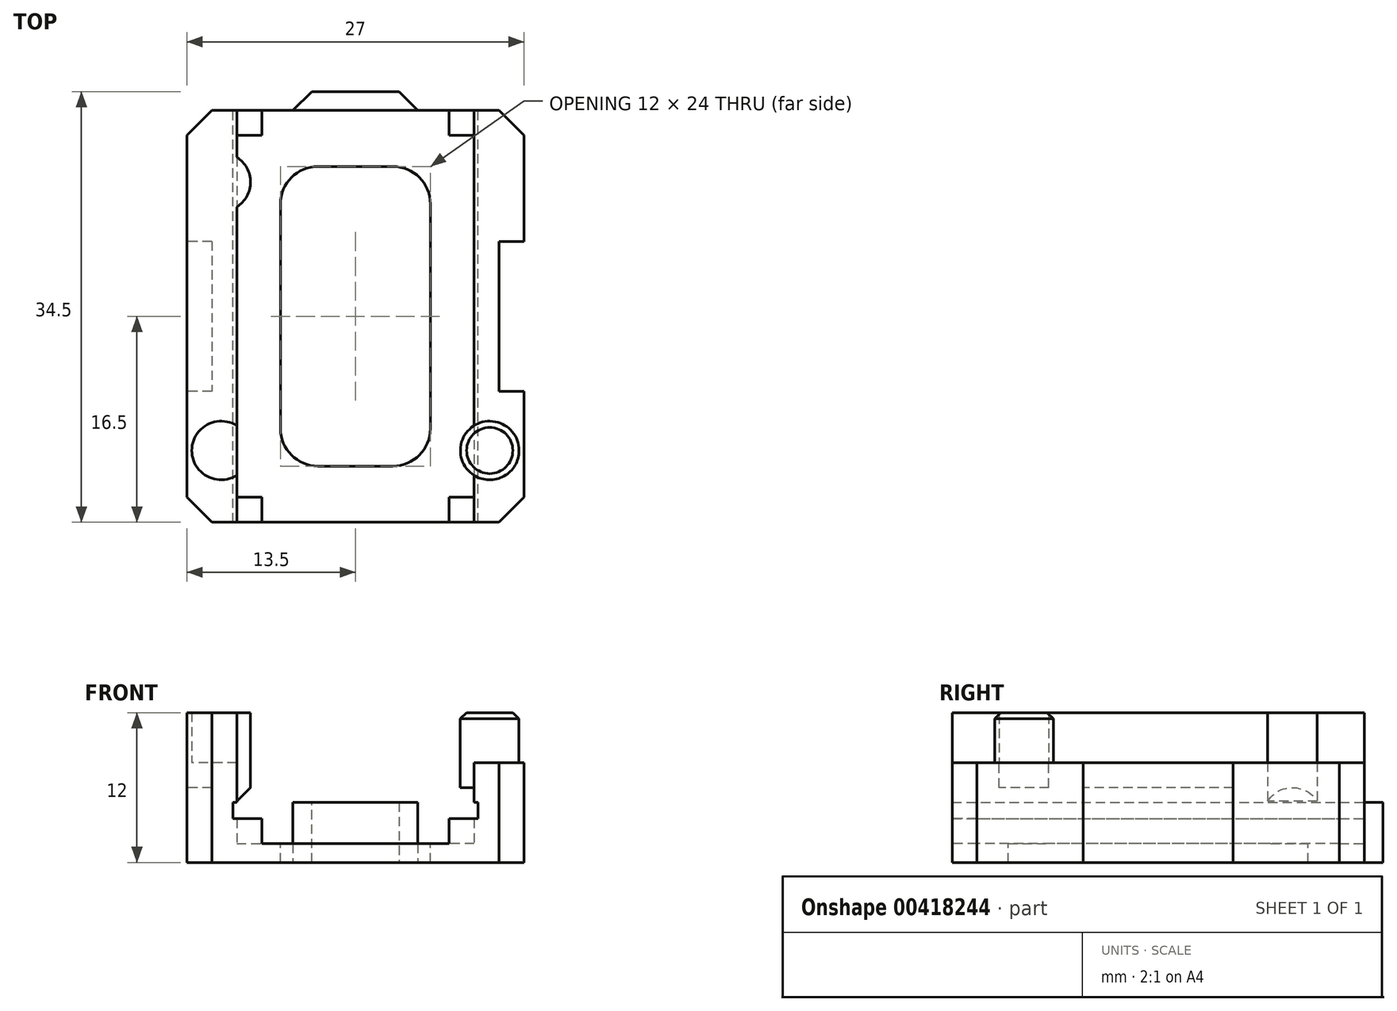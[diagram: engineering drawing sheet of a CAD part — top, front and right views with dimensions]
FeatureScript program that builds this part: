
annotation { "Feature Type Name" : "Feature", "Feature Type Description" : "" }
export const myFeature = defineFeature(function(context is Context, id is Id, definition is map)
    precondition{}
    {
        {
            var Q0;
            Q0=qCreatedBy(makeId("Top.planeOp"),FACE);
            var sketch = newSketch(context, id + "F0", { "sketchPlane" : qUnion([Q0])});
            skLineSegment(sketch, "E0.bottom", {"start": v(13.5, 16.5) * mm, "end": v(-13.5, 16.5) * mm});
            skLineSegment(sketch, "E0.top", {"start": v(13.5, -16.5) * mm, "end": v(-13.5, -16.5) * mm});
            skLineSegment(sketch, "E0.left", {"start": v(13.5, 16.5) * mm, "end": v(13.5, -16.5) * mm});
            skLineSegment(sketch, "E0.right", {"start": v(-13.5, 16.5) * mm, "end": v(-13.5, -16.5) * mm});
            skPoint(sketch, "E0.middle", {"position": v(0, 0) * mm});
            skLineSegment(sketch, "E1", {"start": v(-9.5, 16.5) * mm, "end": v(-9.5, -16.5) * mm});
            skLineSegment(sketch, "E2.MirrorCS", {"start": v(9.5, 16.5) * mm, "end": v(9.5, -16.5) * mm});
            skLineSegment(sketch, "E3", {"start": v(-5, 16.5) * mm, "end": v(-5, 18) * mm});
            skLineSegment(sketch, "E4", {"start": v(-5, 18) * mm, "end": v(0, 18) * mm});
            skLineSegment(sketch, "E5.MirrorCS", {"start": v(5, 18) * mm, "end": v(0, 18) * mm});
            skLineSegment(sketch, "E6.MirrorCS", {"start": v(5, 16.5) * mm, "end": v(5, 18) * mm});
            skSolve(sketch);
        }
        {
            var Q0;
            {var subQ0=sQuery(id+"F0.wireOp",EDGE,"E1");Q0=makeQuery(id+"F0.imprint","IMPRINT",FACE,{"disambiguationData":[TD([[makeQuery(id+"F0.imprint","IMPRINT",EDGE,{"derivedFrom":subQ0}),1.0]])]});}
            extrude(context, id + "F1", {"entities" : qUnion([Q0]), "depth" : 1.5 * mm});
        }
        {
            var Q0;
            {var subQ0=sQuery(id+"F0.wireOp",EDGE,"E0.right");Q0=makeQuery(id+"F0.imprint","IMPRINT",FACE,{"disambiguationData":[TD([[makeQuery(id+"F0.imprint","IMPRINT",EDGE,{"derivedFrom":subQ0}),1.0]])]});}
            var Q1;
            {var subQ0=sQuery(id+"F0.wireOp",EDGE,"E0.left");Q1=makeQuery(id+"F0.imprint","IMPRINT",FACE,{"disambiguationData":[TD([[makeQuery(id+"F0.imprint","IMPRINT",EDGE,{"derivedFrom":subQ0}),-1.0]])]});}
            extrude(context, id + "F2", {"entities" : qUnion([Q0, Q1]), "operationType" : NewBodyOperationType.ADD, "depth" : 8 * mm});
        }
        {
            var Q0;
            Q0=makeQuery(id+"F2.opExtrude","SWEPT_FACE",FACE,{"disambiguationData":[OSD([sQuery(id+"F0.wireOp",EDGE,"E1")])]});
            var sketch = newSketch(context, id + "F3", { "sketchPlane" : qUnion([Q0])});
            skLineSegment(sketch, "E7", {"start": v(-16.5, 3.5) * mm, "end": v(16.5, 3.5) * mm});
            skLineSegment(sketch, "E8", {"start": v(-16.5, 5) * mm, "end": v(16.5, 5) * mm});
            skSolve(sketch);
        }
        {
            var Q0;
            {var subQ0=sQuery(id+"F3.wireOp",EDGE,"E7");Q0=makeQuery(id+"F3.imprint","IMPRINT",FACE,{"disambiguationData":[TD([[makeQuery(id+"F3.imprint","IMPRINT",EDGE,{"derivedFrom":subQ0}),1.0]])]});}
            extrude(context, id + "F4", {"entities" : qUnion([Q0]), "operationType" : NewBodyOperationType.REMOVE, "oppositeDirection" : true, "depth" : 0.5 * mm});
        }
        {
            var Q0;
            Q0=makeQuery(id+"F2.opExtrude","SWEPT_FACE",FACE,{"disambiguationData":[OSD([sQuery(id+"F0.wireOp",EDGE,"E2.MirrorCS")])]});
            var sketch = newSketch(context, id + "F5", { "sketchPlane" : qUnion([Q0])});
            skLineSegment(sketch, "E9", {"start": v(16.5, 3.5) * mm, "end": v(-16.5, 3.5) * mm});
            skLineSegment(sketch, "E10", {"start": v(16.5, 5) * mm, "end": v(-16.5, 5) * mm});
            skSolve(sketch);
        }
        {
            var Q0;
            {var subQ0=sQuery(id+"F5.wireOp",EDGE,"E9");Q0=makeQuery(id+"F5.imprint","IMPRINT",FACE,{"disambiguationData":[TD([[makeQuery(id+"F5.imprint","IMPRINT",EDGE,{"derivedFrom":subQ0}),-1.0]])]});}
            extrude(context, id + "F6", {"entities" : qUnion([Q0]), "operationType" : NewBodyOperationType.REMOVE, "oppositeDirection" : true, "depth" : 0.5 * mm});
        }
        {
            var Q0;
            Q0=makeQuery(id+"F1.opExtrude","CAP_FACE",FACE,{"disambiguationData":[OSD([sQuery(id+"F0.wireOp",EDGE,"E0.bottom"),sQuery(id+"F0.wireOp",EDGE,"E0.top"),sQuery(id+"F0.wireOp",EDGE,"E1"),sQuery(id+"F0.wireOp",EDGE,"E2.MirrorCS")])],"isStart":false});
            var sketch = newSketch(context, id + "F7", { "sketchPlane" : qUnion([Q0])});
            skLineSegment(sketch, "E11", {"start": v(-9.5, 14.5) * mm, "end": v(-7.5, 14.5) * mm});
            skLineSegment(sketch, "E12", {"start": v(-7.5, 14.5) * mm, "end": v(-7.5, 16.5) * mm});
            skLineSegment(sketch, "E13.MirrorCS", {"start": v(7.5, 14.5) * mm, "end": v(7.5, 16.5) * mm});
            skLineSegment(sketch, "E14.MirrorCS", {"start": v(9.5, 14.5) * mm, "end": v(7.5, 14.5) * mm});
            skLineSegment(sketch, "E15.MirrorCS", {"start": v(-9.5, -14.5) * mm, "end": v(-7.5, -14.5) * mm});
            skLineSegment(sketch, "E16.MirrorCS", {"start": v(-7.5, -14.5) * mm, "end": v(-7.5, -16.5) * mm});
            skLineSegment(sketch, "E17.MirrorCS", {"start": v(7.5, -14.5) * mm, "end": v(7.5, -16.5) * mm});
            skLineSegment(sketch, "E18.MirrorCS", {"start": v(9.5, -14.5) * mm, "end": v(7.5, -14.5) * mm});
            skSolve(sketch);
        }
        {
            var Q0;
            {var subQ0=sQuery(id+"F7.wireOp",EDGE,"E11");Q0=makeQuery(id+"F7.imprint","IMPRINT",FACE,{"disambiguationData":[TD([[makeQuery(id+"F7.imprint","IMPRINT",EDGE,{"derivedFrom":subQ0}),1.0]])]});}
            var Q1;
            {var subQ0=sQuery(id+"F7.wireOp",EDGE,"E13.MirrorCS");Q1=makeQuery(id+"F7.imprint","IMPRINT",FACE,{"disambiguationData":[TD([[makeQuery(id+"F7.imprint","IMPRINT",EDGE,{"derivedFrom":subQ0}),-1.0]])]});}
            var Q2;
            {var subQ0=sQuery(id+"F7.wireOp",EDGE,"E17.MirrorCS");Q2=makeQuery(id+"F7.imprint","IMPRINT",FACE,{"disambiguationData":[TD([[makeQuery(id+"F7.imprint","IMPRINT",EDGE,{"derivedFrom":subQ0}),1.0]])]});}
            var Q3;
            {var subQ0=sQuery(id+"F7.wireOp",EDGE,"E15.MirrorCS");Q3=makeQuery(id+"F7.imprint","IMPRINT",FACE,{"disambiguationData":[TD([[makeQuery(id+"F7.imprint","IMPRINT",EDGE,{"derivedFrom":subQ0}),-1.0]])]});}
            extrude(context, id + "F8", {"entities" : qUnion([Q0, Q1, Q2, Q3]), "operationType" : NewBodyOperationType.ADD, "depth" : 2 * mm});
        }
        {
            var Q0;
            Q0=makeQuery(id+"F2.opExtrude","CAP_FACE",FACE,{"disambiguationData":[OSD([sQuery(id+"F0.wireOp",EDGE,"E0.bottom"),sQuery(id+"F0.wireOp",EDGE,"E0.top"),sQuery(id+"F0.wireOp",EDGE,"E0.right"),sQuery(id+"F0.wireOp",EDGE,"E1")])],"isStart":false});
            var sketch = newSketch(context, id + "F9", { "sketchPlane" : qUnion([Q0])});
            skPoint(sketch, "E19.middle", {"position": v(0, 0) * mm});
            skCircle(sketch, "E20", {"center": v(-10.75, 10.75) * mm, "radius": 2.35 * mm});
            skCircle(sketch, "E21.MirrorC", {"center": v(10.75, 10.75) * mm, "radius": 2.35 * mm});
            skCircle(sketch, "E22.MirrorC", {"center": v(-10.75, -10.75) * mm, "radius": 2.35 * mm});
            skCircle(sketch, "E23.MirrorC", {"center": v(10.75, -10.75) * mm, "radius": 2.35 * mm});
            skSolve(sketch);
        }
        {
            var Q0;
            Q0=makeQuery(id+"F1.opExtrude","CAP_FACE",FACE,{"disambiguationData":[OSD([sQuery(id+"F0.wireOp",EDGE,"E0.bottom"),sQuery(id+"F0.wireOp",EDGE,"E0.top"),sQuery(id+"F0.wireOp",EDGE,"E1"),sQuery(id+"F0.wireOp",EDGE,"E2.MirrorCS")])],"isStart":false});
            var sketch = newSketch(context, id + "F10", { "sketchPlane" : qUnion([Q0])});
            skLineSegment(sketch, "E24.bottom", {"start": v(6, 12) * mm, "end": v(-6, 12) * mm});
            skLineSegment(sketch, "E24.top", {"start": v(6, -12) * mm, "end": v(-6, -12) * mm});
            skLineSegment(sketch, "E24.left", {"start": v(6, 12) * mm, "end": v(6, -12) * mm});
            skLineSegment(sketch, "E24.right", {"start": v(-6, 12) * mm, "end": v(-6, -12) * mm});
            skPoint(sketch, "E24.middle", {"position": v(0, 0) * mm});
            skSolve(sketch);
        }
        {
            var Q0;
            Q0=makeQuery(id+"F10.imprint","IMPRINT",FACE,{"disambiguationData":[TD([[makeQuery(id+"F10.imprint","IMPRINT",EDGE,{"derivedFrom":sQuery(id+"F10.wireOp",EDGE,"E24.bottom")}),1.0]])]});
            extrude(context, id + "F11", {"entities" : qUnion([Q0]), "operationType" : NewBodyOperationType.REMOVE, "oppositeDirection" : true, "depth" : 1.5 * mm});
        }
        {
            var Q0;
            Q0=makeQuery(id+"F2.opExtrude","CAP_FACE",FACE,{"disambiguationData":[OSD([sQuery(id+"F0.wireOp",EDGE,"E0.bottom"),sQuery(id+"F0.wireOp",EDGE,"E0.top"),sQuery(id+"F0.wireOp",EDGE,"E0.right"),sQuery(id+"F0.wireOp",EDGE,"E1")])],"isStart":false});
            var sketch = newSketch(context, id + "F12", { "sketchPlane" : qUnion([Q0])});
            skLineSegment(sketch, "E25", {"start": v(-13.5, 6) * mm, "end": v(-11.5, 6) * mm});
            skLineSegment(sketch, "E26", {"start": v(-11.5, 6) * mm, "end": v(-11.5, 0) * mm});
            skLineSegment(sketch, "E27.MirrorCS", {"start": v(13.5, 6) * mm, "end": v(11.5, 6) * mm});
            skLineSegment(sketch, "E28.MirrorCS", {"start": v(11.5, 6) * mm, "end": v(11.5, 0) * mm});
            skLineSegment(sketch, "E29.MirrorCS", {"start": v(-13.5, -6) * mm, "end": v(-11.5, -6) * mm});
            skLineSegment(sketch, "E30.MirrorCS", {"start": v(-11.5, -6) * mm, "end": v(-11.5, 0) * mm});
            skLineSegment(sketch, "E31.MirrorCS", {"start": v(11.5, -6) * mm, "end": v(11.5, 0) * mm});
            skLineSegment(sketch, "E32.MirrorCS", {"start": v(13.5, -6) * mm, "end": v(11.5, -6) * mm});
            skLineSegment(sketch, "E33", {"start": v(13.5, 6) * mm, "end": v(13.5, -6) * mm});
            skSolve(sketch);
        }
        {
            var Q0;
            Q0=makeQuery(id+"F12.imprint","IMPRINT",FACE,{"disambiguationData":[TD([[makeQuery(id+"F12.imprint","IMPRINT",EDGE,{"derivedFrom":sQuery(id+"F12.wireOp",EDGE,"E27.MirrorCS")}),1.0]])]});
            var Q1;
            {var subQ1=sQuery(id+"F12.wireOp",EDGE,"E25");Q1=makeQuery(id+"F12.imprint","IMPRINT",FACE,{"disambiguationData":[TD([[makeQuery(id+"F12.imprint","IMPRINT",EDGE,{"derivedFrom":subQ1}),-1.0]])]});}
            extrude(context, id + "F13", {"entities" : qUnion([Q0, Q1]), "operationType" : NewBodyOperationType.REMOVE, "oppositeDirection" : true, "depth" : 25 * mm});
        }
        {
            var Q0;
            Q0=makeQuery(id+"F11.boolean.opBoolean","COPY",EDGE,{"derivedFrom":makeQuery(id+"F11.opExtrude","SWEPT_EDGE",EDGE,{"disambiguationData":[OSD([sQuery(id+"F10.wireOp",EDGE,"E24.bottom"),sQuery(id+"F10.wireOp",EDGE,"E24.left")])]})});
            var Q1;
            Q1=makeQuery(id+"F11.boolean.opBoolean","COPY",EDGE,{"derivedFrom":makeQuery(id+"F11.opExtrude","SWEPT_EDGE",EDGE,{"disambiguationData":[OSD([sQuery(id+"F10.wireOp",EDGE,"E24.bottom"),sQuery(id+"F10.wireOp",EDGE,"E24.right")])]})});
            var Q2;
            Q2=makeQuery(id+"F11.boolean.opBoolean","COPY",EDGE,{"derivedFrom":makeQuery(id+"F11.opExtrude","SWEPT_EDGE",EDGE,{"disambiguationData":[OSD([sQuery(id+"F10.wireOp",EDGE,"E24.top"),sQuery(id+"F10.wireOp",EDGE,"E24.right")])]})});
            var Q3;
            Q3=makeQuery(id+"F11.boolean.opBoolean","COPY",EDGE,{"derivedFrom":makeQuery(id+"F11.opExtrude","SWEPT_EDGE",EDGE,{"disambiguationData":[OSD([sQuery(id+"F10.wireOp",EDGE,"E24.top"),sQuery(id+"F10.wireOp",EDGE,"E24.left")])]})});
            fillet(context, id + "F14", {"entities" : qUnion([Q0, Q1, Q2, Q3]), "radius" : 3 * mm, "tangentPropagation" : true, "allowEdgeOverflow" : false});
        }
        {
            var Q0;
            {var subQ0=sQuery(id+"F9.wireOp",EDGE,"E20");var subQ1=makeQuery(id+"F2.opExtrude","CAP_EDGE",EDGE,{"disambiguationData":[OSD([sQuery(id+"F0.wireOp",EDGE,"E1")])],"isStart":false});var subQ2=makeQuery(id+"F9.imprint","INTERSECT",VERTEX,{"disambiguationData":[OD(0.0)],"derivedFrom":[subQ1,subQ0]});Q0=makeQuery(id+"F9.imprint","IMPRINT",FACE,{"disambiguationData":[TD([[makeQuery(id+"F9.imprint","IMPRINT",EDGE,{"disambiguationData":[TD([[subQ2,-1.0]])],"derivedFrom":subQ0}),1.0]])]});}
            var Q1;
            Q1=makeQuery(id+"F9.imprint","IMPRINT",FACE,{"disambiguationData":[TD([[makeQuery(id+"F9.imprint","IMPRINT",EDGE,{"derivedFrom":sQuery(id+"F9.wireOp",EDGE,"E21.MirrorC")}),-1.0]])]});
            var Q2;
            {var subQ0=sQuery(id+"F9.wireOp",EDGE,"E22.MirrorC");var subQ1=makeQuery(id+"F2.opExtrude","CAP_EDGE",EDGE,{"disambiguationData":[OSD([sQuery(id+"F0.wireOp",EDGE,"E1")])],"isStart":false});var subQ2=makeQuery(id+"F9.imprint","INTERSECT",VERTEX,{"disambiguationData":[OD(0.0)],"derivedFrom":[subQ1,subQ0]});Q2=makeQuery(id+"F9.imprint","IMPRINT",FACE,{"disambiguationData":[TD([[makeQuery(id+"F9.imprint","IMPRINT",EDGE,{"disambiguationData":[TD([[subQ2,-1.0]])],"derivedFrom":subQ0}),-1.0]])]});}
            var Q3;
            Q3=makeQuery(id+"F9.imprint","IMPRINT",FACE,{"disambiguationData":[TD([[makeQuery(id+"F9.imprint","IMPRINT",EDGE,{"derivedFrom":sQuery(id+"F9.wireOp",EDGE,"E23.MirrorC")}),1.0]])]});
            extrude(context, id + "F15", {"entities" : qUnion([Q0, Q1, Q2, Q3]), "operationType" : NewBodyOperationType.ADD, "depth" : 4 * mm});
        }
        {
            var Q0;
            Q0=makeQuery(id+"F15.opExtrude","CAP_FACE",FACE,{"disambiguationData":[OSD([sQuery(id+"F9.wireOp",EDGE,"E23.MirrorC")])],"isStart":true});
            var Q1;
            Q1=makeQuery(id+"F15.opExtrude","CAP_FACE",FACE,{"disambiguationData":[OSD([sQuery(id+"F9.wireOp",EDGE,"E21.MirrorC")])],"isStart":true});
            extrude(context, id + "F16", {"entities" : qUnion([Q0, Q1]), "operationType" : NewBodyOperationType.ADD, "depth" : 2 * mm});
        }
        {
            var Q0;
            {var subQ0=sQuery(id+"F9.wireOp",EDGE,"E22.MirrorC");var subQ1=makeQuery(id+"F2.opExtrude","CAP_EDGE",EDGE,{"disambiguationData":[OSD([sQuery(id+"F0.wireOp",EDGE,"E1")])],"isStart":false});var subQ2=makeQuery(id+"F9.imprint","INTERSECT",VERTEX,{"disambiguationData":[OD(0.0)],"derivedFrom":[subQ1,subQ0]});Q0=makeQuery(id+"F9.imprint","IMPRINT",FACE,{"disambiguationData":[TD([[makeQuery(id+"F9.imprint","IMPRINT",EDGE,{"disambiguationData":[TD([[subQ2,1.0]])],"derivedFrom":subQ0}),-1.0]])]});}
            var Q1;
            {var subQ0=sQuery(id+"F9.wireOp",EDGE,"E20");var subQ1=makeQuery(id+"F2.opExtrude","CAP_EDGE",EDGE,{"disambiguationData":[OSD([sQuery(id+"F0.wireOp",EDGE,"E1")])],"isStart":false});var subQ2=makeQuery(id+"F9.imprint","INTERSECT",VERTEX,{"disambiguationData":[OD(0.0)],"derivedFrom":[subQ1,subQ0]});Q1=makeQuery(id+"F9.imprint","IMPRINT",FACE,{"disambiguationData":[TD([[makeQuery(id+"F9.imprint","IMPRINT",EDGE,{"disambiguationData":[TD([[subQ2,1.0]])],"derivedFrom":subQ0}),1.0]])]});}
            extrude(context, id + "F17", {"entities" : qUnion([Q0, Q1]), "operationType" : NewBodyOperationType.ADD, "depth" : 4 * mm, "hasSecondDirection" : true, "secondDirectionOppositeDirection" : true, "secondDirectionDepth" : 2 * mm});
        }
        {
            var Q0;
            Q0=makeQuery(id+"F4.boolean.opBoolean","COPY",FACE,{"derivedFrom":makeQuery(id+"F4.opExtrude","SWEPT_FACE",FACE,{"disambiguationData":[OSD([sQuery(id+"F3.wireOp",EDGE,"E8")])]})});
            var Q1;
            Q1=makeQuery(id+"F6.boolean.opBoolean","COPY",FACE,{"derivedFrom":makeQuery(id+"F6.opExtrude","SWEPT_FACE",FACE,{"disambiguationData":[OSD([sQuery(id+"F5.wireOp",EDGE,"E10")])]})});
            extrude(context, id + "F18", {"entities" : qUnion([Q0, Q1]), "operationType" : NewBodyOperationType.ADD, "depth" : 0.2 * mm});
        }
        {
            var Q0;
            Q0=makeQuery(id+"F4.boolean.opBoolean","COPY",FACE,{"derivedFrom":makeQuery(id+"F4.opExtrude","CAP_FACE",FACE,{"disambiguationData":[OSD([sQuery(id+"F0.wireOp",EDGE,"E0.bottom"),sQuery(id+"F0.wireOp",EDGE,"E0.top"),sQuery(id+"F0.wireOp",EDGE,"E1"),sQuery(id+"F3.wireOp",EDGE,"E7"),sQuery(id+"F3.wireOp",EDGE,"E8")])],"isStart":false})});
            extrude(context, id + "F19", {"entities" : qUnion([Q0]), "operationType" : NewBodyOperationType.ADD, "depth" : 0.2 * mm});
        }
        {
            var Q0;
            Q0=makeQuery(id+"F6.boolean.opBoolean","COPY",FACE,{"derivedFrom":makeQuery(id+"F6.opExtrude","CAP_FACE",FACE,{"disambiguationData":[OSD([sQuery(id+"F0.wireOp",EDGE,"E0.bottom"),sQuery(id+"F0.wireOp",EDGE,"E0.top"),sQuery(id+"F0.wireOp",EDGE,"E2.MirrorCS"),sQuery(id+"F5.wireOp",EDGE,"E9"),sQuery(id+"F5.wireOp",EDGE,"E10")])],"isStart":false})});
            extrude(context, id + "F20", {"entities" : qUnion([Q0]), "operationType" : NewBodyOperationType.ADD, "depth" : 0.2 * mm});
        }
        {
            var Q0;
            Q0=makeQuery(id+"F15.opExtrude","CAP_EDGE",EDGE,{"disambiguationData":[OSD([sQuery(id+"F9.wireOp",EDGE,"E21.MirrorC")])],"isStart":false});
            var Q1;
            Q1=makeQuery(id+"F15.opExtrude","CAP_EDGE",EDGE,{"disambiguationData":[OSD([sQuery(id+"F9.wireOp",EDGE,"E23.MirrorC")])],"isStart":false});
            var Q2;
            {var subQ0=sQuery(id+"F9.wireOp",EDGE,"E22.MirrorC");Q2=makeQuery(id+"F17.boolean.opBoolean","MERGE",EDGE,{"derivedFrom":[makeQuery(id+"F15.opExtrude","CAP_EDGE",EDGE,{"disambiguationData":[OSD([subQ0])],"isStart":false}),makeQuery(id+"F17.opExtrude","CAP_EDGE",EDGE,{"disambiguationData":[OSD([subQ0])],"isStart":false})]});}
            var Q3;
            {var subQ0=sQuery(id+"F9.wireOp",EDGE,"E20");Q3=makeQuery(id+"F17.boolean.opBoolean","MERGE",EDGE,{"derivedFrom":[makeQuery(id+"F15.opExtrude","CAP_EDGE",EDGE,{"disambiguationData":[OSD([subQ0])],"isStart":false}),makeQuery(id+"F17.opExtrude","CAP_EDGE",EDGE,{"disambiguationData":[OSD([subQ0])],"isStart":false})]});}
            chamfer(context, id + "F21", {"entities" : qUnion([Q0, Q1, Q2, Q3]), "width" : 0.5 * mm, "tangentPropagation" : true});
        }
        {
            var Q0;
            {var subQ0=sQuery(id+"F9.wireOp",EDGE,"E22.MirrorC");var subQ1=sQuery(id+"F0.wireOp",EDGE,"E1");var subQ2=makeQuery(id+"F2.opExtrude","CAP_EDGE",EDGE,{"disambiguationData":[OSD([subQ1])],"isStart":false});Q0=makeQuery(id+"F17.opExtrude","CAP_EDGE",EDGE,{"disambiguationData":[OSD([subQ1]),TDD([makeQuery(id+"F9.imprint","IMPRINT",EDGE,{"disambiguationData":[TD([[makeQuery(id+"F9.imprint","INTERSECT",VERTEX,{"disambiguationData":[OD(0.0)],"derivedFrom":[subQ2,subQ0]}),1.0]])],"derivedFrom":subQ2})])],"isStart":true});}
            var Q1;
            {var subQ0=sQuery(id+"F9.wireOp",EDGE,"E20");var subQ1=sQuery(id+"F0.wireOp",EDGE,"E1");var subQ2=makeQuery(id+"F2.opExtrude","CAP_EDGE",EDGE,{"disambiguationData":[OSD([subQ1])],"isStart":false});Q1=makeQuery(id+"F17.opExtrude","CAP_EDGE",EDGE,{"disambiguationData":[OSD([subQ1]),TDD([makeQuery(id+"F9.imprint","IMPRINT",EDGE,{"disambiguationData":[TD([[makeQuery(id+"F9.imprint","INTERSECT",VERTEX,{"disambiguationData":[OD(0.0)],"derivedFrom":[subQ2,subQ0]}),-1.0]])],"derivedFrom":subQ2})])],"isStart":true});}
            var Q2;
            {var subQ0=sQuery(id+"F0.wireOp",EDGE,"E2.MirrorCS");Q2=makeQuery(id+"F16.opExtrude","CAP_EDGE",EDGE,{"disambiguationData":[OSD([subQ0]),TDD([makeQuery(id+"F15.boolean.opBoolean","SPLIT",EDGE,{"disambiguationData":[topologyDisambiguationEdgeConnected([makeQuery(id+"F2.opExtrude","SWEPT_FACE",FACE,{"disambiguationData":[OSD([subQ0])]}),makeQuery(id+"F15.opExtrude","CAP_FACE",FACE,{"disambiguationData":[OSD([sQuery(id+"F9.wireOp",EDGE,"E23.MirrorC")])],"isStart":true})])],"derivedFrom":makeQuery(id+"F2.opExtrude","CAP_EDGE",EDGE,{"disambiguationData":[OSD([subQ0])],"isStart":false})})])],"isStart":false});}
            var Q3;
            {var subQ0=sQuery(id+"F0.wireOp",EDGE,"E2.MirrorCS");Q3=makeQuery(id+"F16.opExtrude","CAP_EDGE",EDGE,{"disambiguationData":[OSD([subQ0]),TDD([makeQuery(id+"F15.boolean.opBoolean","SPLIT",EDGE,{"disambiguationData":[topologyDisambiguationEdgeConnected([makeQuery(id+"F2.opExtrude","SWEPT_FACE",FACE,{"disambiguationData":[OSD([subQ0])]}),makeQuery(id+"F15.opExtrude","CAP_FACE",FACE,{"disambiguationData":[OSD([sQuery(id+"F9.wireOp",EDGE,"E21.MirrorC")])],"isStart":true})])],"derivedFrom":makeQuery(id+"F2.opExtrude","CAP_EDGE",EDGE,{"disambiguationData":[OSD([subQ0])],"isStart":false})})])],"isStart":false});}
            chamfer(context, id + "F22", {"entities" : qUnion([Q0, Q1, Q2, Q3]), "width" : 1.1 * mm, "tangentPropagation" : true});
        }
        {
            var Q0;
            {var subQ0=sQuery(id+"F0.wireOp",EDGE,"E3");Q0=makeQuery(id+"F0.imprint","IMPRINT",FACE,{"disambiguationData":[TD([[makeQuery(id+"F0.imprint","IMPRINT",EDGE,{"derivedFrom":subQ0}),-1.0]])]});}
            var Q1;
            Q1=makeQuery(id+"F18.opExtrude","CAP_FACE",FACE,{"disambiguationData":[OSD([sQuery(id+"F3.wireOp",EDGE,"E8")])],"isStart":false});
            extrude(context, id + "F23", {"entities" : qUnion([Q0]), "operationType" : NewBodyOperationType.ADD, "endBound" : BoundingType.UP_TO_SURFACE, "endBoundEntityFace" : qUnion([Q1]), "depth" : 25 * mm});
        }
        {
            var Q0;
            Q0=makeQuery(id+"F23.opExtrude","SWEPT_EDGE",EDGE,{"disambiguationData":[OSD([sQuery(id+"F0.wireOp",EDGE,"E3"),sQuery(id+"F0.wireOp",EDGE,"E4")])]});
            var Q1;
            Q1=makeQuery(id+"F23.opExtrude","SWEPT_EDGE",EDGE,{"disambiguationData":[OSD([sQuery(id+"F0.wireOp",EDGE,"E5.MirrorCS"),sQuery(id+"F0.wireOp",EDGE,"E6.MirrorCS")])]});
            chamfer(context, id + "F24", {"entities" : qUnion([Q0, Q1]), "width" : 1.5 * mm, "tangentPropagation" : true});
        }
        {
            var Q0;
            Q0=makeQuery(id+"F2.opExtrude","SWEPT_EDGE",EDGE,{"disambiguationData":[OSD([sQuery(id+"F0.wireOp",EDGE,"E0.top"),sQuery(id+"F0.wireOp",EDGE,"E0.left")])]});
            var Q1;
            Q1=makeQuery(id+"F2.opExtrude","SWEPT_EDGE",EDGE,{"disambiguationData":[OSD([sQuery(id+"F0.wireOp",EDGE,"E0.top"),sQuery(id+"F0.wireOp",EDGE,"E0.right")])]});
            var Q2;
            Q2=makeQuery(id+"F2.opExtrude","SWEPT_EDGE",EDGE,{"disambiguationData":[OSD([sQuery(id+"F0.wireOp",EDGE,"E0.bottom"),sQuery(id+"F0.wireOp",EDGE,"E0.left")])]});
            var Q3;
            Q3=makeQuery(id+"F2.opExtrude","SWEPT_EDGE",EDGE,{"disambiguationData":[OSD([sQuery(id+"F0.wireOp",EDGE,"E0.bottom"),sQuery(id+"F0.wireOp",EDGE,"E0.right")])]});
            chamfer(context, id + "F25", {"entities" : qUnion([Q0, Q1, Q2, Q3]), "width" : 2 * mm, "tangentPropagation" : true});
        }
    });
